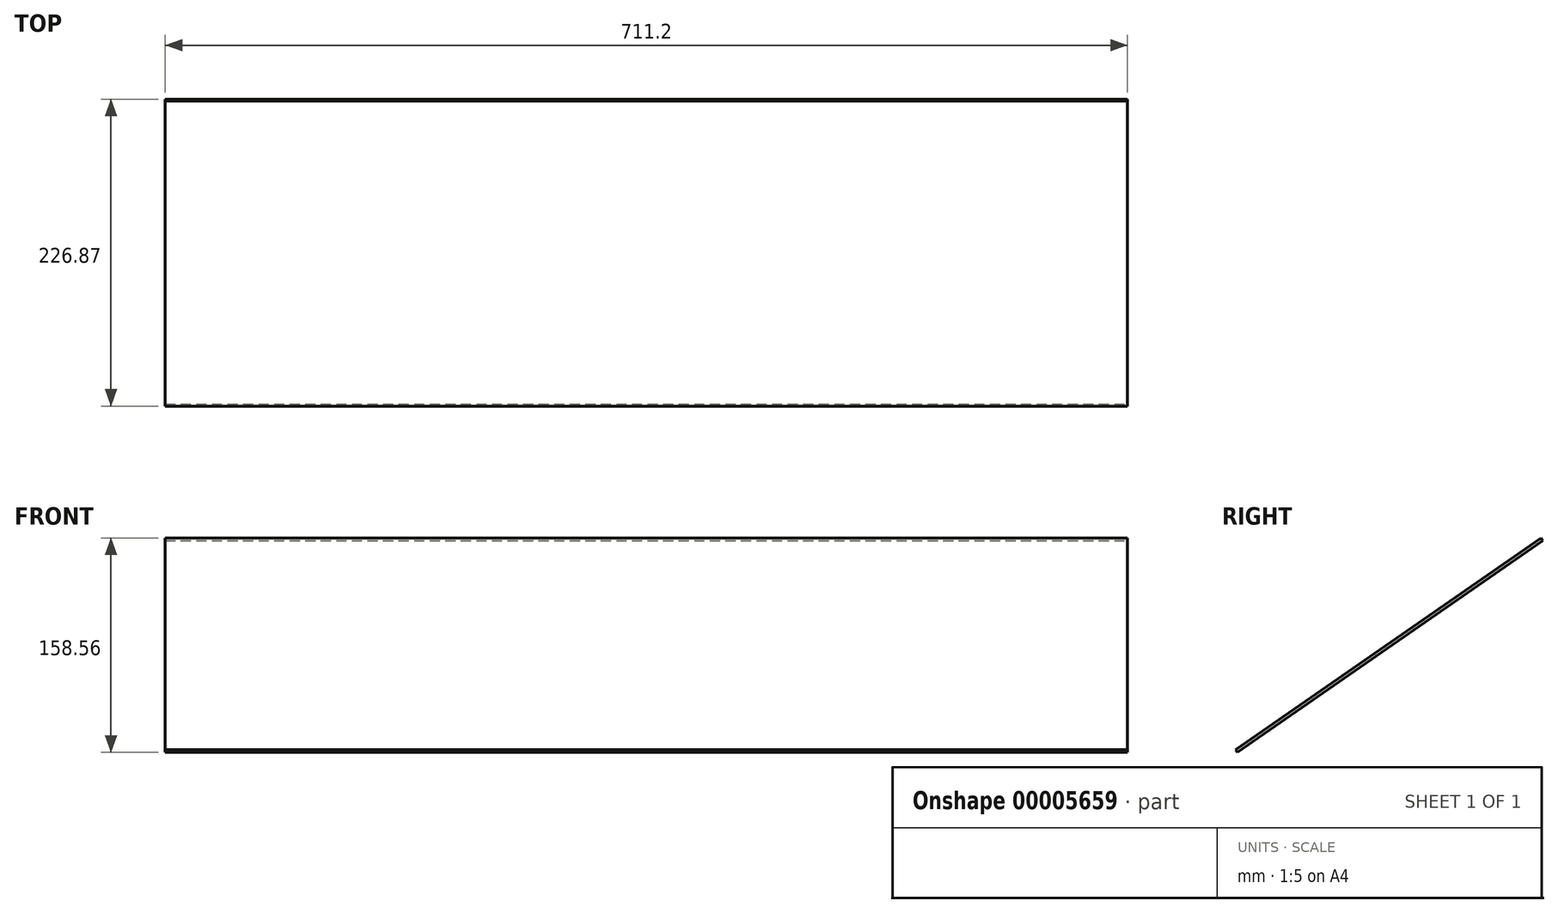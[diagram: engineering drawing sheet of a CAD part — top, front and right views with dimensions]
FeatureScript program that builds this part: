
annotation { "Feature Type Name" : "Feature", "Feature Type Description" : "" }
export const myFeature = defineFeature(function(context is Context, id is Id, definition is map)
    precondition{}
    {
        {
            var Q0;
            Q0=qCreatedBy(makeId("Right.planeOp"),FACE);
            var sketch = newSketch(context, id + "F0", { "sketchPlane" : qUnion([Q0])});
            skLineSegment(sketch, "E0", {"start": v(0, 0) * mm, "end": v(225.53, 156.62) * mm});
            skLineSegment(sketch, "E1", {"start": v(225.53, 156.62) * mm, "end": v(226.87, 154.68) * mm});
            skLineSegment(sketch, "E2", {"start": v(226.87, 154.68) * mm, "end": v(1.35, -1.94) * mm});
            skLineSegment(sketch, "E3", {"start": v(1.35, -1.94) * mm, "end": v(0, 0) * mm});
            skLineSegment(sketch, "E4", {"start": v(0, 0) * mm, "end": v(55.19, 0) * mm, "construction": true});
            skSolve(sketch);
        }
        {
            var Q0;
            Q0 = qSketchRegion(id + "F0", true);
            extrude(context, id + "F1", {"entities" : qUnion([Q0]), "oppositeDirection" : true, "depth" : 711.2 * mm});
        }
    });
